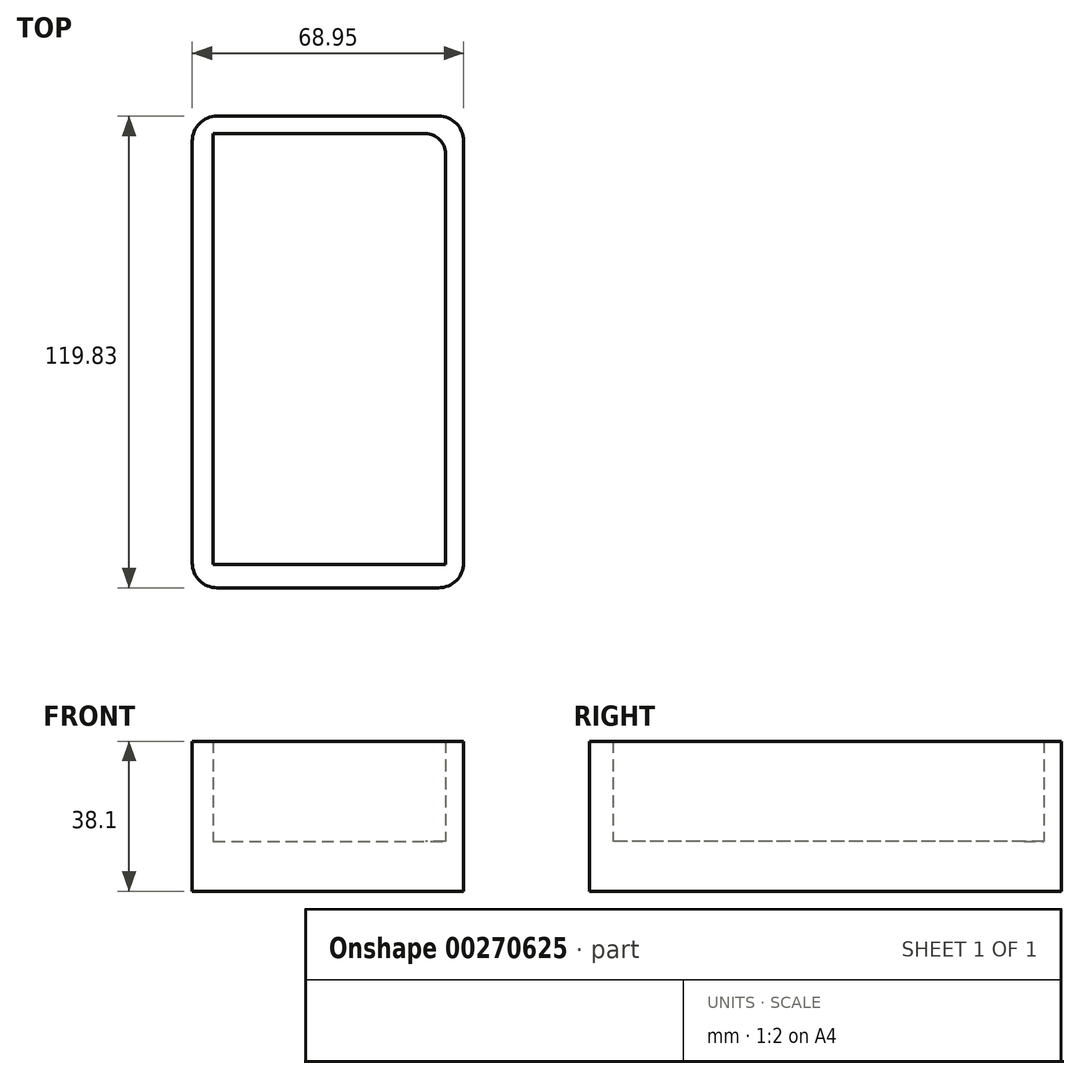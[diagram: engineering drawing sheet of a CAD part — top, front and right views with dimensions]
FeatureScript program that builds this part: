
annotation { "Feature Type Name" : "Feature", "Feature Type Description" : "" }
export const myFeature = defineFeature(function(context is Context, id is Id, definition is map)
    precondition{}
    {
        {
            var Q0;
            Q0=qCreatedBy(makeId("Top.planeOp"),FACE);
            var sketch = newSketch(context, id + "F0", { "sketchPlane" : qUnion([Q0])});
            skLineSegment(sketch, "E0.bottom", {"start": v(-6.35, -64.34) * mm, "end": v(-62.6, -64.34) * mm});
            skLineSegment(sketch, "E0.top", {"start": v(-6.35, 55.5) * mm, "end": v(-62.6, 55.5) * mm});
            skLineSegment(sketch, "E0.left", {"start": v(0, -57.99) * mm, "end": v(0, 49.14) * mm});
            skLineSegment(sketch, "E0.right", {"start": v(-68.95, -57.99) * mm, "end": v(-68.95, 49.14) * mm});
            skLineSegment(sketch, "E1.bottom", {"start": v(-63.6, 51.07) * mm, "end": v(-4.6, 51.07) * mm});
            skLineSegment(sketch, "E1.top", {"start": v(-63.6, -58.44) * mm, "end": v(-4.6, -58.44) * mm});
            skLineSegment(sketch, "E1.left", {"start": v(-63.6, 51.07) * mm, "end": v(-63.6, -58.44) * mm});
            skLineSegment(sketch, "E1.right", {"start": v(-4.6, 51.07) * mm, "end": v(-4.6, -58.44) * mm});
            skPoint(sketch, "E2.visualSharp", {"position": v(-68.95, 55.5) * mm});
            skArc(sketch, "E2.filletArc", {"start": v(-62.6, 55.5) * mm, "mid": v(-67.09, 53.63) * mm, "end": v(-68.95, 49.14) * mm});
            skPoint(sketch, "E3.visualSharp", {"position": v(0, 55.5) * mm});
            skArc(sketch, "E3.filletArc", {"start": v(0, 49.14) * mm, "mid": v(-1.86, 53.63) * mm, "end": v(-6.35, 55.5) * mm});
            skPoint(sketch, "E4.visualSharp", {"position": v(0, -64.34) * mm});
            skArc(sketch, "E4.filletArc", {"start": v(-6.35, -64.34) * mm, "mid": v(-1.86, -62.48) * mm, "end": v(0, -57.99) * mm});
            skPoint(sketch, "E5.visualSharp", {"position": v(-68.95, -64.34) * mm});
            skArc(sketch, "E5.filletArc", {"start": v(-68.95, -57.99) * mm, "mid": v(-67.09, -62.48) * mm, "end": v(-62.6, -64.34) * mm});
            skSolve(sketch);
        }
        {
            var Q0;
            Q0=makeQuery(id+"F0.imprint","IMPRINT",FACE,{"disambiguationData":[TD([[makeQuery(id+"F0.imprint","IMPRINT",EDGE,{"derivedFrom":sQuery(id+"F0.wireOp",EDGE,"E0.bottom")}),-1.0]])]});
            extrude(context, id + "F1", {"entities" : qUnion([Q0]), "depth" : 38.1 * mm});
        }
        {
            var Q0;
            Q0=makeQuery(id+"F0.imprint","IMPRINT",FACE,{"disambiguationData":[TD([[makeQuery(id+"F0.imprint","IMPRINT",EDGE,{"derivedFrom":sQuery(id+"F0.wireOp",EDGE,"E1.bottom")}),-1.0]])]});
            extrude(context, id + "F2", {"entities" : qUnion([Q0]), "operationType" : NewBodyOperationType.ADD, "depth" : 12.7 * mm});
        }
        {
            var Q0;
            Q0=makeQuery(id+"F1.opExtrude","SWEPT_EDGE",EDGE,{"disambiguationData":[OSD([sQuery(id+"F0.wireOp",EDGE,"E1.bottom"),sQuery(id+"F0.wireOp",EDGE,"E1.right")])]});
            fillet(context, id + "F3", {"entities" : qUnion([Q0]), "radius" : 5.08 * mm, "tangentPropagation" : true, "allowEdgeOverflow" : false});
        }
    });
